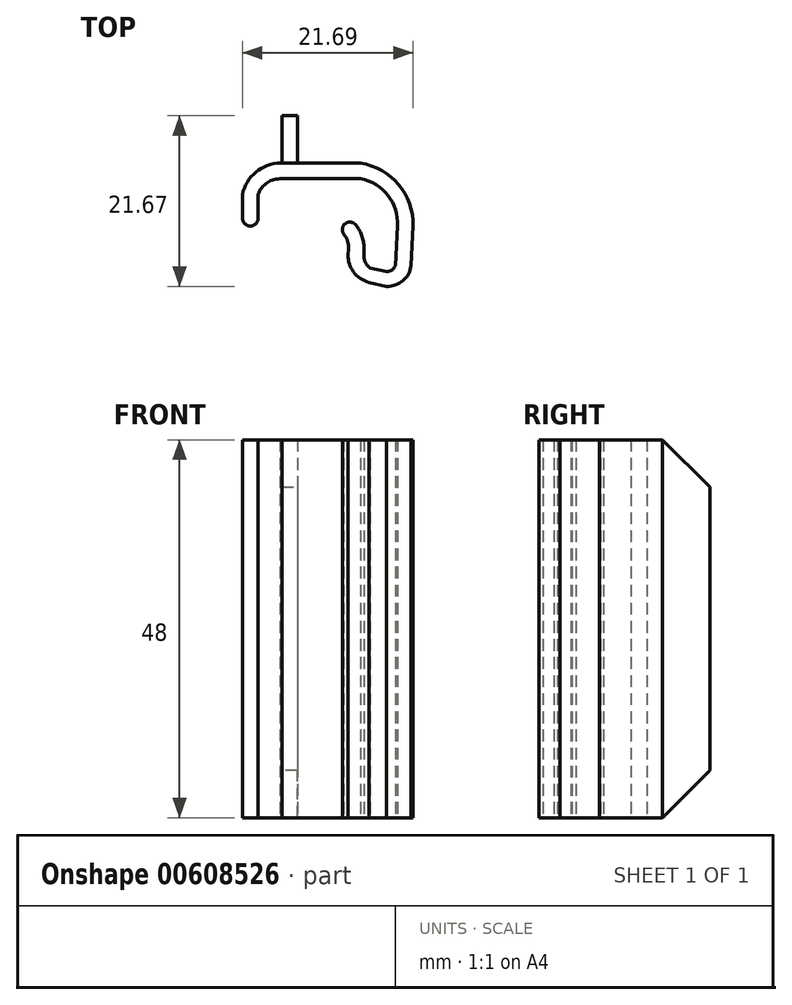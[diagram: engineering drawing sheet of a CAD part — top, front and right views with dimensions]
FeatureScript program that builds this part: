
annotation { "Feature Type Name" : "Feature", "Feature Type Description" : "" }
export const myFeature = defineFeature(function(context is Context, id is Id, definition is map)
    precondition{}
    {
        {
            var Q0;
            Q0=qCreatedBy(makeId("Top.planeOp"),FACE);
            var sketch = newSketch(context, id + "F0", { "sketchPlane" : qUnion([Q0])});
            skLineSegment(sketch, "E0.bottom", {"start": v(0, 0) * mm, "end": v(2, 0) * mm});
            skLineSegment(sketch, "E0.left", {"start": v(0, 0) * mm, "end": v(0, 4) * mm});
            skLineSegment(sketch, "E0.right", {"start": v(2, 0) * mm, "end": v(2, 4) * mm});
            skLineSegment(sketch, "E1.bottom", {"start": v(4.8, 8) * mm, "end": v(5, 8) * mm});
            skLineSegment(sketch, "E1.top", {"start": v(4.6, 6) * mm, "end": v(15, 6) * mm});
            skLineSegment(sketch, "E2", {"start": v(21.42, -5) * mm, "end": v(21.69, 0) * mm});
            skLineSegment(sketch, "E3", {"start": v(19.42, -5) * mm, "end": v(19.69, 0.1) * mm});
            skLineSegment(sketch, "E4", {"start": v(18.27, -7.66) * mm, "end": v(16.07, -7.16) * mm});
            skLineSegment(sketch, "E5", {"start": v(16.19, -5.33) * mm, "end": v(18.27, -5.8) * mm});
            skLineSegment(sketch, "E6", {"start": v(13.42, -3.64) * mm, "end": v(13.47, -2.6) * mm});
            skLineSegment(sketch, "E7", {"start": v(15.45, -3) * mm, "end": v(15.41, -3.8) * mm});
            skLineSegment(sketch, "E8", {"start": v(12.67, -0.84) * mm, "end": v(12.35, -0.59) * mm});
            skPoint(sketch, "E9", {"position": v(15, 8) * mm});
            skPoint(sketch, "E10", {"position": v(21.69, 0) * mm});
            skArc(sketch, "E11", {"start": v(21.69, 0) * mm, "mid": v(19.82, 5.24) * mm, "end": v(15, 8) * mm});
            skPoint(sketch, "E12", {"position": v(15, 6) * mm});
            skPoint(sketch, "E13", {"position": v(19.68, 0) * mm});
            skArc(sketch, "E14", {"start": v(19.68, 0) * mm, "mid": v(18.48, 3.89) * mm, "end": v(15, 6) * mm});
            skPoint(sketch, "E15", {"position": v(5, 8) * mm});
            skPoint(sketch, "E16", {"position": v(0, 4) * mm});
            skArc(sketch, "E17", {"start": v(5, 8) * mm, "mid": v(1.78, 6.9) * mm, "end": v(0, 4) * mm});
            skPoint(sketch, "E18", {"position": v(2, 4) * mm});
            skPoint(sketch, "E19", {"position": v(5, 6) * mm});
            skArc(sketch, "E20", {"start": v(5, 6) * mm, "mid": v(3.16, 5.5) * mm, "end": v(2, 4) * mm});
            skPoint(sketch, "E21", {"position": v(21.42, -5) * mm});
            skPoint(sketch, "E22", {"position": v(18.27, -7.66) * mm});
            skPoint(sketch, "E23", {"position": v(19.42, -5) * mm});
            skArc(sketch, "E24", {"start": v(18.27, -7.66) * mm, "mid": v(20.38, -6.96) * mm, "end": v(21.42, -5) * mm});
            skPoint(sketch, "E25", {"position": v(18.27, -5.8) * mm});
            skArc(sketch, "E26", {"start": v(18.27, -5.8) * mm, "mid": v(18.97, -5.58) * mm, "end": v(19.42, -5) * mm});
            skPoint(sketch, "E27.orphan", {"position": v(21.27, -8) * mm});
            skPoint(sketch, "E28", {"position": v(15.43, -3.5) * mm});
            skPoint(sketch, "E29", {"position": v(16.19, -5.33) * mm});
            skPoint(sketch, "E30", {"position": v(16.19, -7.18) * mm});
            skPoint(sketch, "E31", {"position": v(13.42, -3.5) * mm});
            skArc(sketch, "E32", {"start": v(13.42, -3.5) * mm, "mid": v(14.12, -5.87) * mm, "end": v(16.19, -7.18) * mm});
            skArc(sketch, "E33", {"start": v(15.43, -3.5) * mm, "mid": v(15.56, -4.52) * mm, "end": v(16.19, -5.33) * mm});
            skPoint(sketch, "E34.orphan", {"position": v(13.27, -6.5) * mm});
            skPoint(sketch, "E35", {"position": v(12.35, -0.59) * mm});
            skPoint(sketch, "E36", {"position": v(13.45, -3) * mm});
            skArc(sketch, "E37", {"start": v(13.45, -3) * mm, "mid": v(13.25, -1.64) * mm, "end": v(12.35, -0.59) * mm});
            skPoint(sketch, "E38", {"position": v(15.45, -3) * mm});
            skArc(sketch, "E39", {"start": v(15.45, -3) * mm, "mid": v(14.97, -0.76) * mm, "end": v(13.53, 1.03) * mm});
            skPoint(sketch, "E40.orphan", {"position": v(13.53, -1.5) * mm});
            skLineSegment(sketch, "E41.top", {"start": v(5, 14) * mm, "end": v(7, 14) * mm});
            skLineSegment(sketch, "E41.left", {"start": v(5, 8) * mm, "end": v(5, 14) * mm});
            skLineSegment(sketch, "E41.right", {"start": v(7, 8) * mm, "end": v(7, 14) * mm});
            skLineSegment(sketch, "E42.trimOffspring", {"start": v(7, 8) * mm, "end": v(15, 8) * mm});
            skLineSegment(sketch, "E43", {"start": v(12.35, -0.59) * mm, "end": v(13.53, 1.03) * mm});
            skSolve(sketch);
        }
        {
            var Q0;
            Q0=makeQuery(id+"F0.imprint","IMPRINT",FACE,{"disambiguationData":[TD([[makeQuery(id+"F0.imprint","IMPRINT",EDGE,{"derivedFrom":sQuery(id+"F0.wireOp",EDGE,"E0.bottom")}),1.0]])]});
            extrude(context, id + "F1", {"entities" : qUnion([Q0]), "depth" : 48 * mm, "offsetDistance" : 25 * mm});
        }
        {
            var Q0;
            Q0=makeQuery(id+"F1.opExtrude","CAP_EDGE",EDGE,{"disambiguationData":[OSD([sQuery(id+"F0.wireOp",EDGE,"E41.top")])],"isStart":false});
            var Q1;
            Q1=makeQuery(id+"F1.opExtrude","CAP_EDGE",EDGE,{"disambiguationData":[OSD([sQuery(id+"F0.wireOp",EDGE,"E41.top")])],"isStart":true});
            chamfer(context, id + "F2", {"entities" : qUnion([Q0, Q1]), "width" : 6 * mm, "tangentPropagation" : true});
        }
        {
            var Q0;
            Q0=makeQuery(id+"F1.opExtrude","SWEPT_EDGE",EDGE,{"disambiguationData":[OSD([sQuery(id+"F0.wireOp",EDGE,"E0.bottom"),sQuery(id+"F0.wireOp",EDGE,"E0.left")])]});
            var Q1;
            Q1=makeQuery(id+"F1.opExtrude","SWEPT_EDGE",EDGE,{"disambiguationData":[OSD([sQuery(id+"F0.wireOp",EDGE,"E0.bottom"),sQuery(id+"F0.wireOp",EDGE,"E0.right")])]});
            var Q2;
            Q2=makeQuery(id+"F1.opExtrude","SWEPT_EDGE",EDGE,{"disambiguationData":[OSD([sQuery(id+"F0.wireOp",EDGE,"E8"),sQuery(id+"F0.wireOp",EDGE,"Z7rNZeaN-gbPM-T2jd-6BbT-l8eddshnl254")])]});
            var Q3;
            Q3=makeQuery(id+"F1.opExtrude","SWEPT_EDGE",EDGE,{"disambiguationData":[OSD([sQuery(id+"F0.wireOp",EDGE,"Z7rNZeaN-gbPM-T2jd-6BbT-l8eddshnl254"),sQuery(id+"F0.wireOp",EDGE,"0LRtTv0v-6hfo-n3h5-fgKH-vQcrn3gExEGf")])]});
            var Q4;
            Q4=makeQuery(id+"F1.opExtrude","SWEPT_EDGE",EDGE,{"disambiguationData":[OSD([sQuery(id+"F0.wireOp",EDGE,"E39"),sQuery(id+"F0.wireOp",EDGE,"E43")])]});
            fillet(context, id + "F3", {"entities" : qUnion([Q0, Q1, Q2, Q3, Q4]), "radius" : 1 * mm, "tangentPropagation" : true, "allowEdgeOverflow" : false});
        }
    });
